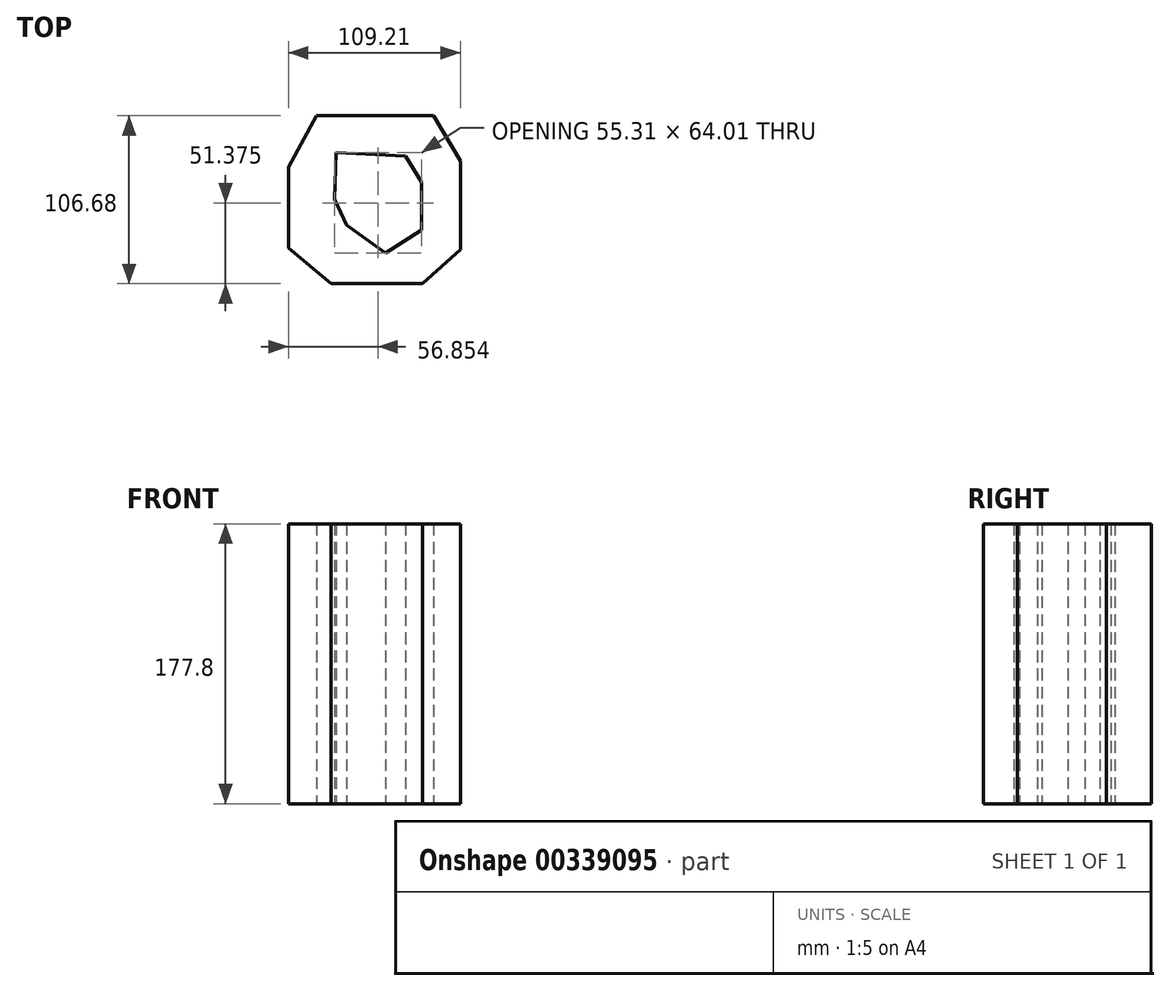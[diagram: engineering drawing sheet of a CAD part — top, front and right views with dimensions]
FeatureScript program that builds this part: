
annotation { "Feature Type Name" : "Feature", "Feature Type Description" : "" }
export const myFeature = defineFeature(function(context is Context, id is Id, definition is map)
    precondition{}
    {
        {
            var Q0;
            Q0=qCreatedBy(makeId("Top.planeOp"),FACE);
            var sketch = newSketch(context, id + "F0", { "sketchPlane" : qUnion([Q0])});
            skLineSegment(sketch, "E0", {"start": v(-37.76, 42.11) * mm, "end": v(36.64, 42.11) * mm});
            skLineSegment(sketch, "E1", {"start": v(36.64, 42.11) * mm, "end": v(53.76, 13.48) * mm});
            skLineSegment(sketch, "E2", {"start": v(53.76, 13.48) * mm, "end": v(53.76, -42.95) * mm});
            skLineSegment(sketch, "E3", {"start": v(53.76, -42.95) * mm, "end": v(29.62, -64.57) * mm});
            skLineSegment(sketch, "E4", {"start": v(29.62, -64.57) * mm, "end": v(-28.5, -64.57) * mm});
            skLineSegment(sketch, "E5", {"start": v(-28.5, -64.57) * mm, "end": v(-55.45, -41.83) * mm});
            skLineSegment(sketch, "E6", {"start": v(-55.45, -41.83) * mm, "end": v(-55.45, 9.55) * mm});
            skLineSegment(sketch, "E7", {"start": v(-55.45, 9.55) * mm, "end": v(-37.76, 42.11) * mm});
            skLineSegment(sketch, "E8", {"start": v(-25.13, 18.8) * mm, "end": v(18.95, 16.56) * mm});
            skLineSegment(sketch, "E9", {"start": v(18.95, 16.56) * mm, "end": v(29.06, 0) * mm});
            skLineSegment(sketch, "E10", {"start": v(29.06, 0) * mm, "end": v(29.06, -30.32) * mm});
            skLineSegment(sketch, "E11", {"start": v(29.06, -30.32) * mm, "end": v(6.32, -45.2) * mm});
            skLineSegment(sketch, "E12", {"start": v(6.32, -45.2) * mm, "end": v(-18.67, -27.23) * mm});
            skLineSegment(sketch, "E13", {"start": v(-18.67, -27.23) * mm, "end": v(-26.25, -10.95) * mm});
            skLineSegment(sketch, "E14", {"start": v(-26.25, -10.95) * mm, "end": v(-25.13, 18.8) * mm});
            skSolve(sketch);
        }
        {
            var Q0;
            Q0=makeQuery(id+"F0.imprint","IMPRINT",FACE,{"disambiguationData":[TD([[makeQuery(id+"F0.imprint","IMPRINT",EDGE,{"derivedFrom":sQuery(id+"F0.wireOp",EDGE,"E0")}),-1.0]])]});
            extrude(context, id + "F1", {"entities" : qUnion([Q0]), "depth" : 177.8 * mm});
        }
    });
